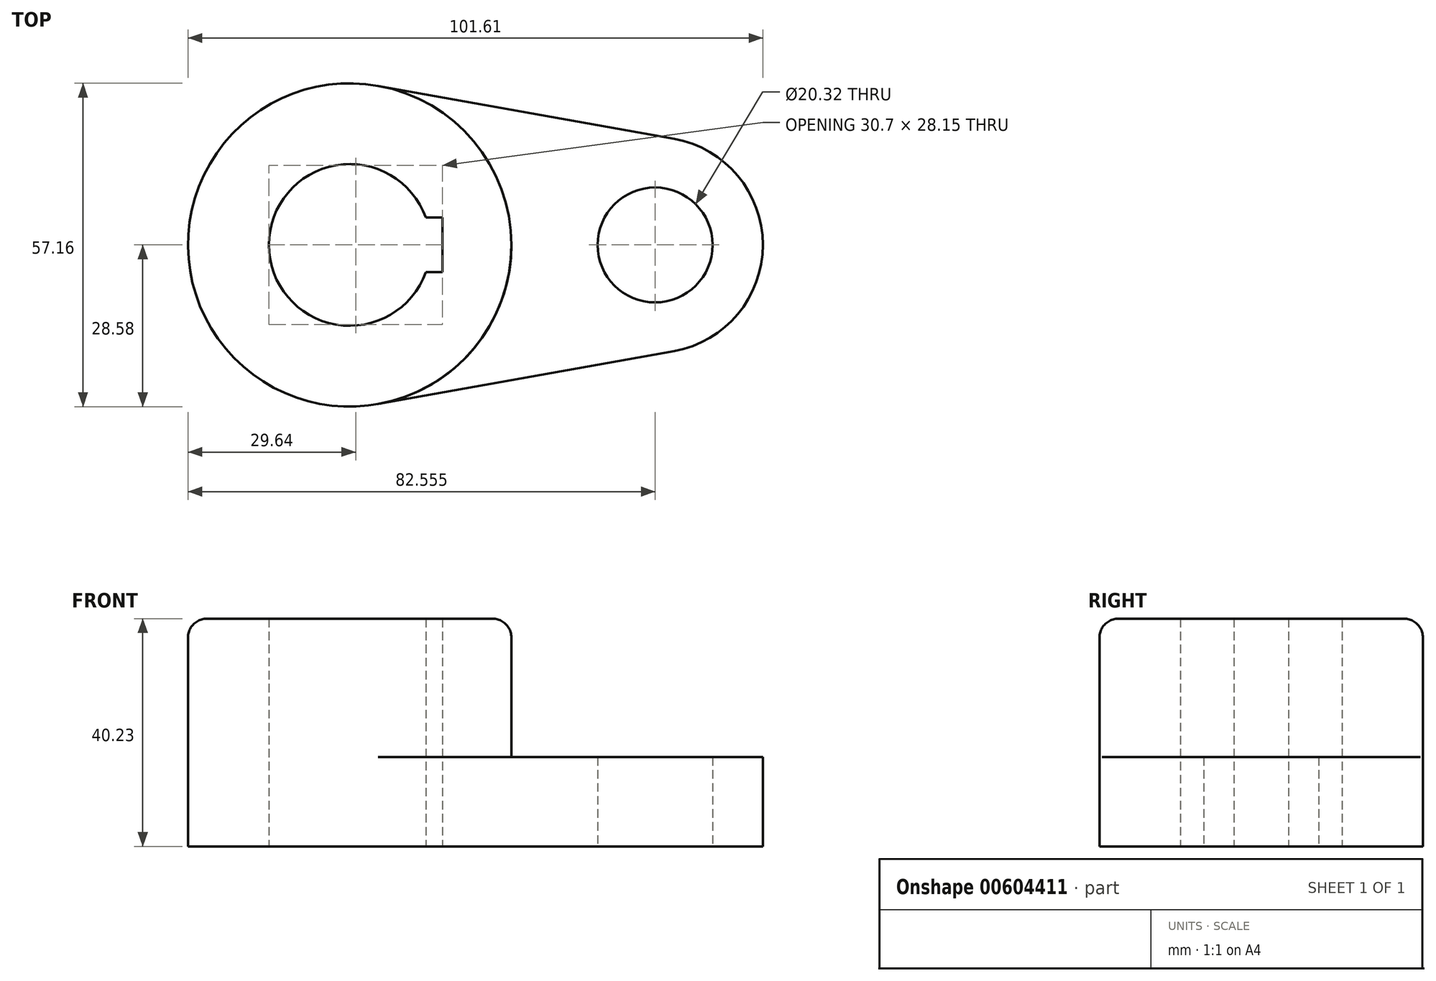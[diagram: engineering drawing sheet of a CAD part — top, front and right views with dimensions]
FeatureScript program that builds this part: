
annotation { "Feature Type Name" : "Feature", "Feature Type Description" : "" }
export const myFeature = defineFeature(function(context is Context, id is Id, definition is map)
    precondition{}
    {
        {
            var Q0;
            Q0=qCreatedBy(makeId("Top.planeOp"),FACE);
            var sketch = newSketch(context, id + "F0", { "sketchPlane" : qUnion([Q0])});
            skCircle(sketch, "E0", {"center": v(0, 0) * mm, "radius": 28.58 * mm});
            skArc(sketch, "E1", {"start": v(13.45, 4.83) * mm, "mid": v(-14.29, 0) * mm, "end": v(13.45, -4.83) * mm});
            skLineSegment(sketch, "E2.bottom", {"start": v(16.4, 4.83) * mm, "end": v(13.45, 4.83) * mm});
            skLineSegment(sketch, "E2.top", {"start": v(16.4, -4.83) * mm, "end": v(13.45, -4.83) * mm});
            skLineSegment(sketch, "E2.left", {"start": v(16.4, 4.83) * mm, "end": v(16.4, -4.83) * mm});
            skLineSegment(sketch, "E3", {"start": v(5.04, 28.13) * mm, "end": v(57.34, 18.75) * mm});
            skLineSegment(sketch, "E4", {"start": v(5.04, -28.13) * mm, "end": v(57.34, -18.75) * mm});
            skArc(sketch, "E5", {"start": v(57.34, -18.75) * mm, "mid": v(73.03, 0) * mm, "end": v(57.34, 18.75) * mm});
            skCircle(sketch, "E6", {"center": v(53.98, 0) * mm, "radius": 10.16 * mm});
            skSolve(sketch);
        }
        {
            var Q0;
            Q0=makeQuery(id+"F0.imprint","IMPRINT",FACE,{"disambiguationData":[TD([[makeQuery(id+"F0.imprint","IMPRINT",EDGE,{"derivedFrom":sQuery(id+"F0.wireOp",EDGE,"E1")}),-1.0]])]});
            extrude(context, id + "F1", {"entities" : qUnion([Q0]), "depth" : 40.23 * mm, "offsetDistance" : 25.4 * mm});
        }
        {
            var Q0;
            Q0 = qSketchRegion(id + "F0", true);
            extrude(context, id + "F2", {"entities" : qUnion([Q0]), "operationType" : NewBodyOperationType.ADD, "depth" : 15.77 * mm, "offsetDistance" : 25.4 * mm});
        }
        {
            var Q0;
            Q0=makeQuery(id+"F1.opExtrude","CAP_EDGE",EDGE,{"disambiguationData":[OSD([sQuery(id+"F0.wireOp",EDGE,"E0")])],"isStart":false});
            fillet(context, id + "F3", {"entities" : qUnion([Q0]), "radius" : 3.3 * mm, "tangentPropagation" : true, "allowEdgeOverflow" : false});
        }
    });
